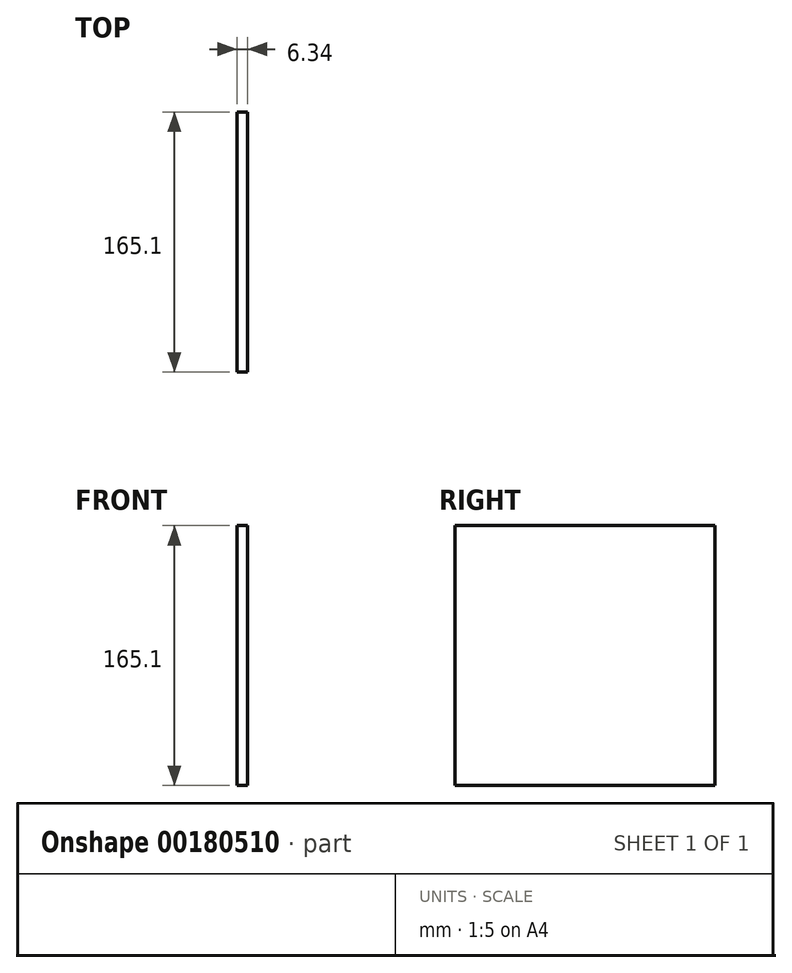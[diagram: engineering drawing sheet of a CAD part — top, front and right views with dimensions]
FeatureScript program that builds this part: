
annotation { "Feature Type Name" : "Feature", "Feature Type Description" : "" }
export const myFeature = defineFeature(function(context is Context, id is Id, definition is map)
    precondition{}
    {
        {
            var Q0;
            Q0=qCreatedBy(makeId("Right.planeOp"),FACE);
            var sketch = newSketch(context, id + "F0", { "sketchPlane" : qUnion([Q0])});
            skLineSegment(sketch, "E0.bottom", {"start": v(82.55, 82.55) * mm, "end": v(-82.55, 82.55) * mm});
            skLineSegment(sketch, "E0.top", {"start": v(82.55, -82.55) * mm, "end": v(-82.55, -82.55) * mm});
            skLineSegment(sketch, "E0.left", {"start": v(82.55, 82.55) * mm, "end": v(82.55, -82.55) * mm});
            skLineSegment(sketch, "E0.right", {"start": v(-82.55, 82.55) * mm, "end": v(-82.55, -82.55) * mm});
            skPoint(sketch, "E0.middle", {"position": v(0, 0) * mm});
            skSolve(sketch);
        }
        {
            var Q0;
            Q0 = qSketchRegion(id + "F0", true);
            extrude(context, id + "F1", {"entities" : qUnion([Q0]), "endBound" : BoundingType.SYMMETRIC, "depth" : 6.35 * mm});
        }
    });
